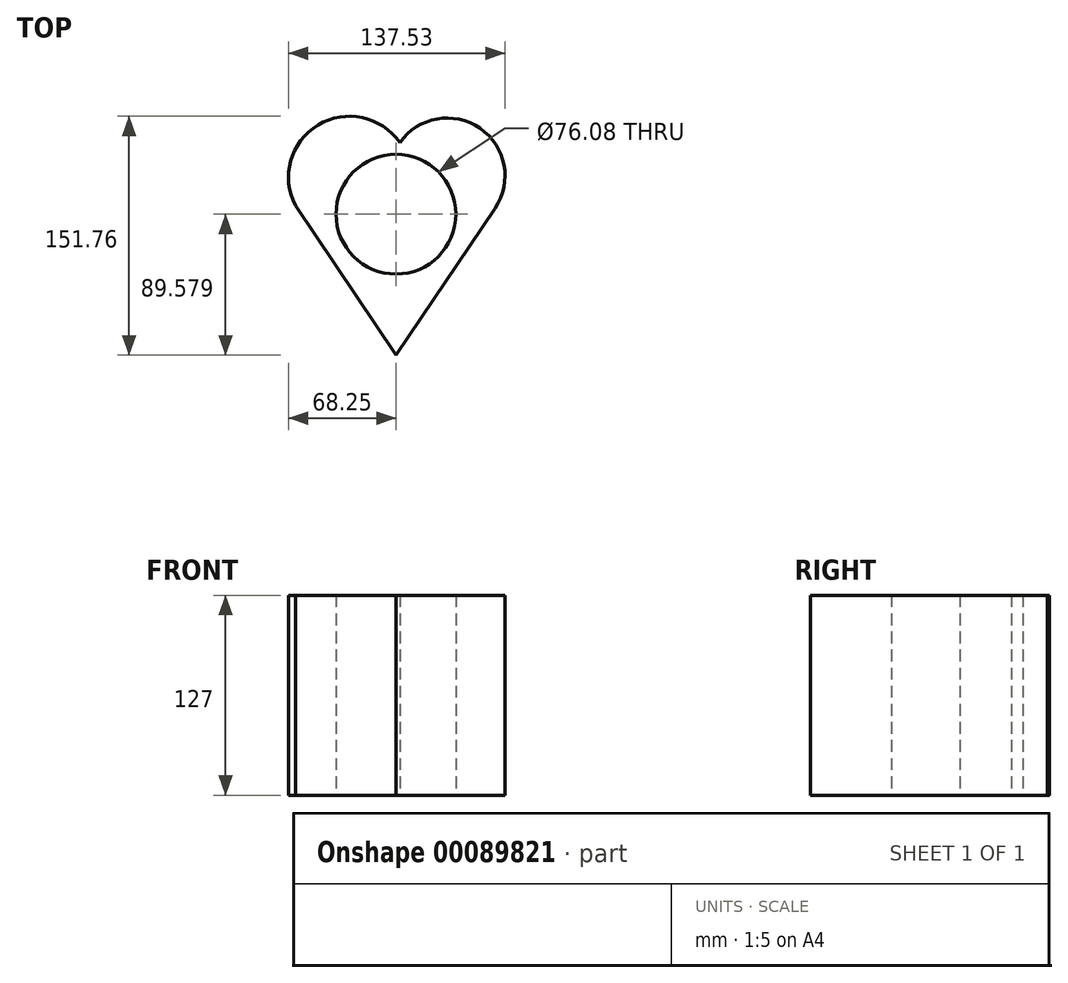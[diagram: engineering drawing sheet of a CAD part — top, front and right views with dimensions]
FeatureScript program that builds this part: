
annotation { "Feature Type Name" : "Feature", "Feature Type Description" : "" }
export const myFeature = defineFeature(function(context is Context, id is Id, definition is map)
    precondition{}
    {
        {
            var Q0;
            Q0=qCreatedBy(makeId("Top.planeOp"),FACE);
            var sketch = newSketch(context, id + "F0", { "sketchPlane" : qUnion([Q0])});
            skArc(sketch, "E0", {"start": v(62.98, 17.83) * mm, "mid": v(53.38, 68.69) * mm, "end": v(2.43, 59.61) * mm});
            skArc(sketch, "E1", {"start": v(2.43, 59.61) * mm, "mid": v(-53.06, 68.29) * mm, "end": v(-59.08, 12.44) * mm});
            skLineSegment(sketch, "E2", {"start": v(-63.84, 19.53) * mm, "end": v(0, -75.46) * mm});
            skLineSegment(sketch, "E3", {"start": v(0, -75.46) * mm, "end": v(62.98, 17.83) * mm});
            skCircle(sketch, "E4", {"center": v(0, 14.12) * mm, "radius": 38.04 * mm});
            skSolve(sketch);
        }
        {
            var Q0;
            {var subQ5=sQuery(id+"F0.wireOp",EDGE,"E0");Q0=makeQuery(id+"F0.imprint","IMPRINT",FACE,{"disambiguationData":[TD([[makeQuery(id+"F0.imprint","IMPRINT",EDGE,{"derivedFrom":subQ5}),1.0]])]});}
            extrude(context, id + "F1", {"entities" : qUnion([Q0]), "depth" : 127 * mm});
        }
    });
